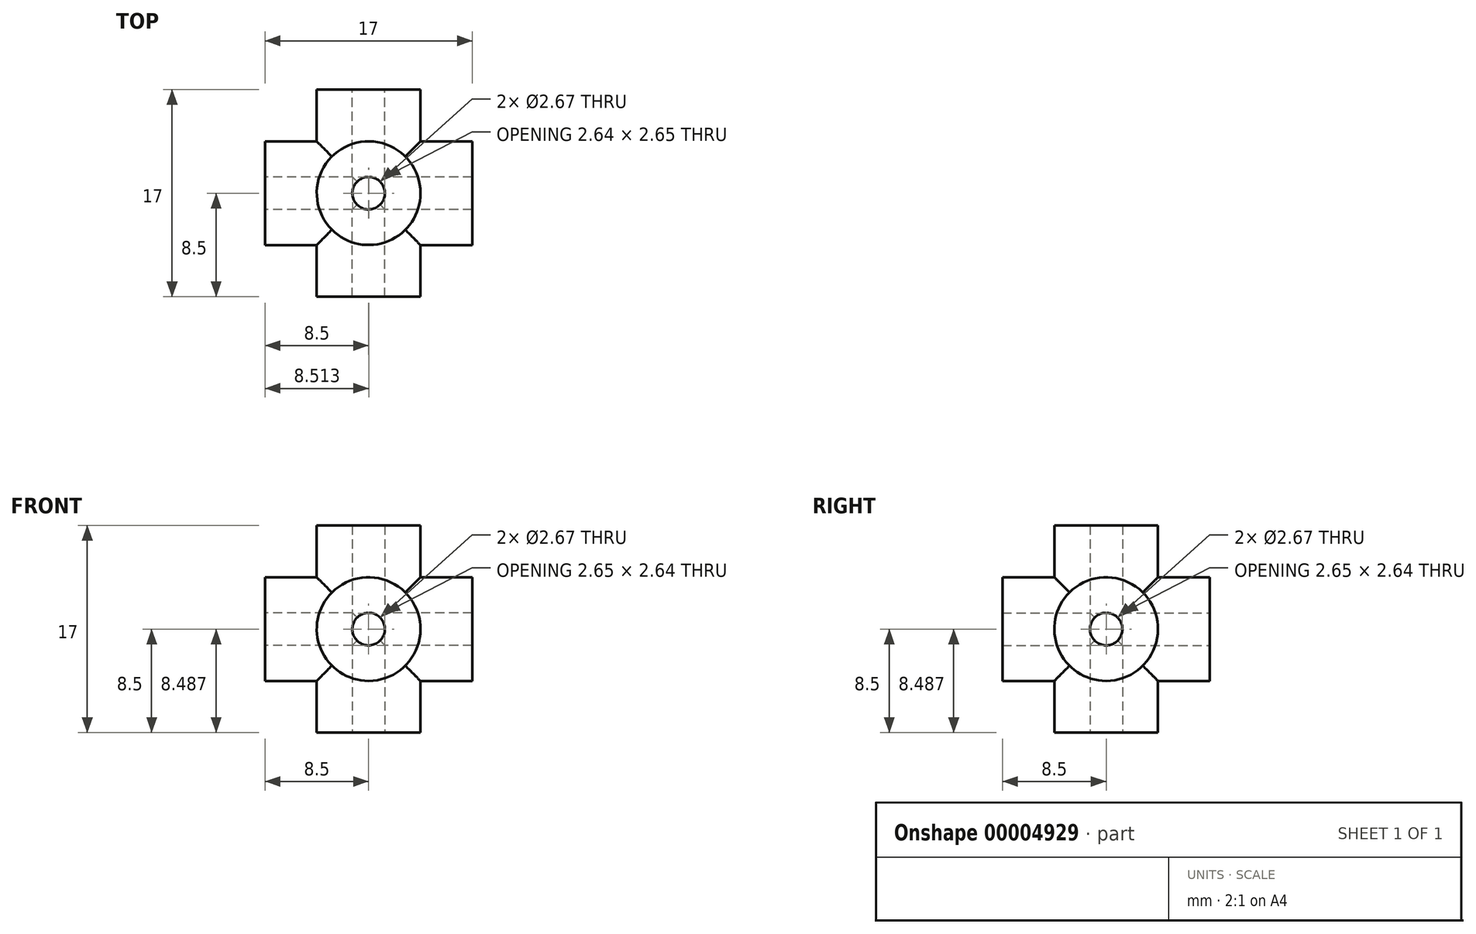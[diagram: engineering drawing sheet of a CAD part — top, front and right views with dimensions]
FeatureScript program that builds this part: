
annotation { "Feature Type Name" : "Feature", "Feature Type Description" : "" }
export const myFeature = defineFeature(function(context is Context, id is Id, definition is map)
    precondition{}
    {
        {
            var Q0;
            Q0=qCreatedBy(makeId("Front.planeOp"),FACE);
            var sketch = newSketch(context, id + "F0", { "sketchPlane" : qUnion([Q0])});
            skCircle(sketch, "E0", {"center": v(0, 0) * mm, "radius": 1.33 * mm});
            skCircle(sketch, "E1", {"center": v(0, 0) * mm, "radius": 4.25 * mm});
            skSolve(sketch);
        }
        {
            var Q0;
            Q0=qCreatedBy(makeId("Right.planeOp"),FACE);
            var sketch = newSketch(context, id + "F1", { "sketchPlane" : qUnion([Q0])});
            skCircle(sketch, "E2", {"center": v(0, 0) * mm, "radius": 1.33 * mm});
            skCircle(sketch, "E3", {"center": v(0, 0) * mm, "radius": 4.25 * mm});
            skSolve(sketch);
        }
        {
            var Q0;
            Q0=qCreatedBy(makeId("Top.planeOp"),FACE);
            var sketch = newSketch(context, id + "F2", { "sketchPlane" : qUnion([Q0])});
            skCircle(sketch, "E4", {"center": v(0, 0) * mm, "radius": 1.33 * mm});
            skCircle(sketch, "E5", {"center": v(0, 0) * mm, "radius": 4.25 * mm});
            skSolve(sketch);
        }
        {
            var Q0;
            Q0 = qSketchRegion(id + "F0", true);
            extrude(context, id + "F3", {"entities" : qUnion([Q0]), "endBound" : BoundingType.SYMMETRIC, "depth" : 17 * mm});
        }
        {
            var Q0;
            Q0=makeQuery(id+"F1.imprint","IMPRINT",FACE,{"disambiguationData":[TD([[makeQuery(id+"F1.imprint","IMPRINT",EDGE,{"derivedFrom":sQuery(id+"F1.wireOp",EDGE,"E2")}),-1.0]])]});
            extrude(context, id + "F4", {"entities" : qUnion([Q0]), "operationType" : NewBodyOperationType.ADD, "endBound" : BoundingType.SYMMETRIC, "depth" : 17 * mm});
        }
        {
            var Q0;
            Q0=makeQuery(id+"F2.imprint","IMPRINT",FACE,{"disambiguationData":[TD([[makeQuery(id+"F2.imprint","IMPRINT",EDGE,{"derivedFrom":sQuery(id+"F2.wireOp",EDGE,"E4")}),-1.0]])]});
            extrude(context, id + "F5", {"entities" : qUnion([Q0]), "operationType" : NewBodyOperationType.ADD, "endBound" : BoundingType.SYMMETRIC, "depth" : 17 * mm});
        }
        {
            var Q0;
            Q0=makeQuery(id+"F0.imprint","IMPRINT",FACE,{"disambiguationData":[TD([[makeQuery(id+"F0.imprint","IMPRINT",EDGE,{"derivedFrom":sQuery(id+"F0.wireOp",EDGE,"E0")}),1.0]])]});
            extrude(context, id + "F6", {"entities" : qUnion([Q0]), "operationType" : NewBodyOperationType.REMOVE, "endBound" : BoundingType.SYMMETRIC, "oppositeDirection" : true, "depth" : 17 * mm});
        }
        {
            var Q0;
            Q0=makeQuery(id+"F5.opExtrude","CAP_FACE",FACE,{"disambiguationData":[OSD([sQuery(id+"F2.wireOp",EDGE,"E4"),sQuery(id+"F2.wireOp",EDGE,"E5")])],"isStart":false});
            var sketch = newSketch(context, id + "F7", { "sketchPlane" : qUnion([Q0])});
            skCircle(sketch, "E6.0", {"center": v(0, 0) * mm, "radius": 1.33 * mm});
            skSolve(sketch);
        }
        {
            var Q0;
            Q0 = qSketchRegion(id + "F7", true);
            extrude(context, id + "F8", {"entities" : qUnion([Q0]), "operationType" : NewBodyOperationType.REMOVE, "endBound" : BoundingType.THROUGH_ALL, "oppositeDirection" : true, "depth" : 25 * mm});
        }
        {
            var Q0;
            Q0=makeQuery(id+"F1.imprint","IMPRINT",FACE,{"disambiguationData":[TD([[makeQuery(id+"F1.imprint","IMPRINT",EDGE,{"derivedFrom":sQuery(id+"F1.wireOp",EDGE,"E2")}),1.0]])]});
            extrude(context, id + "F9", {"entities" : qUnion([Q0]), "operationType" : NewBodyOperationType.REMOVE, "endBound" : BoundingType.SYMMETRIC, "oppositeDirection" : true, "depth" : 17 * mm});
        }
        {
            var Q0;
            Q0=makeQuery(id+"F2.imprint","IMPRINT",FACE,{"disambiguationData":[TD([[makeQuery(id+"F2.imprint","IMPRINT",EDGE,{"derivedFrom":sQuery(id+"F2.wireOp",EDGE,"E4")}),1.0]])]});
            extrude(context, id + "F10", {"entities" : qUnion([Q0]), "operationType" : NewBodyOperationType.REMOVE, "endBound" : BoundingType.SYMMETRIC, "oppositeDirection" : true, "depth" : 17 * mm});
        }
    });
